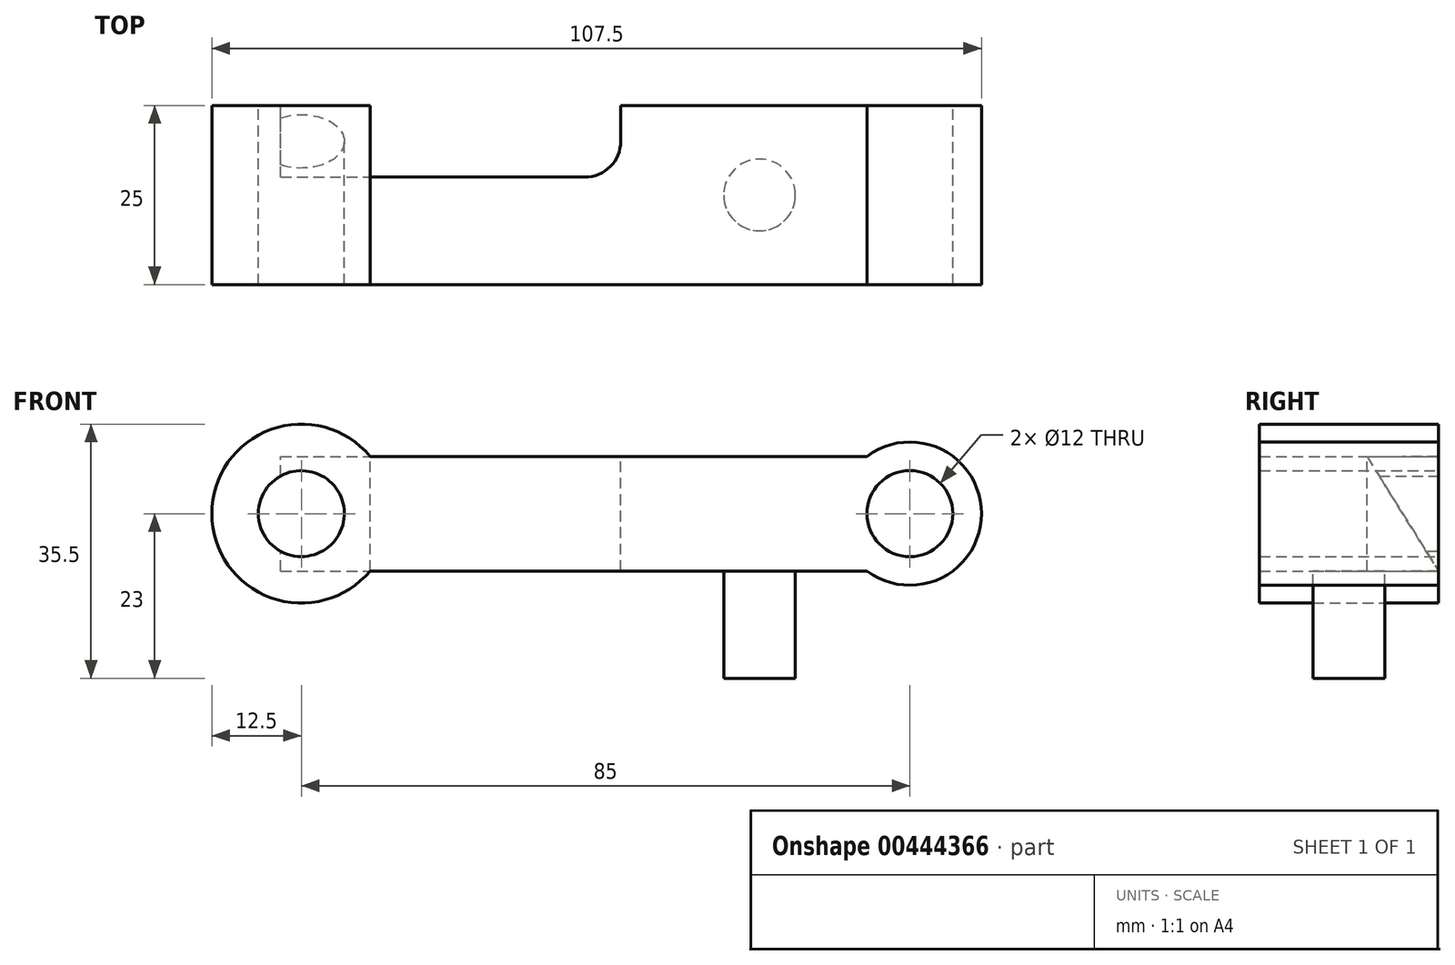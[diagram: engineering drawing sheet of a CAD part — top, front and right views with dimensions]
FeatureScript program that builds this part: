
annotation { "Feature Type Name" : "Feature", "Feature Type Description" : "" }
export const myFeature = defineFeature(function(context is Context, id is Id, definition is map)
    precondition{}
    {
        {
            var Q0;
            Q0=qCreatedBy(makeId("Front.planeOp"),FACE);
            var sketch = newSketch(context, id + "F0", { "sketchPlane" : qUnion([Q0])});
            skCircle(sketch, "E0", {"center": v(0, 0) * mm, "radius": 12.5 * mm});
            skCircle(sketch, "E1", {"center": v(85, 0) * mm, "radius": 10 * mm});
            skLineSegment(sketch, "E2", {"start": v(0, 0) * mm, "end": v(85, 0) * mm, "construction": true});
            skLineSegment(sketch, "E3", {"start": v(9.6, 8) * mm, "end": v(79, 8) * mm});
            skLineSegment(sketch, "E4.MirrorCS", {"start": v(9.6, -8) * mm, "end": v(79, -8) * mm});
            skCircle(sketch, "E5", {"center": v(0, 0) * mm, "radius": 6 * mm});
            skCircle(sketch, "E6", {"center": v(85, 0) * mm, "radius": 6 * mm});
            skSolve(sketch);
        }
        {
            var Q0;
            Q0 = qSketchRegion(id + "F0", true);
            extrude(context, id + "F1", {"entities" : qUnion([Q0]), "depth" : 25 * mm});
        }
        {
            var Q0;
            Q0=makeQuery(id+"F1.opExtrude","SWEPT_FACE",FACE,{"disambiguationData":[OSD([sQuery(id+"F0.wireOp",EDGE,"E3")])]});
            var sketch = newSketch(context, id + "F2", { "sketchPlane" : qUnion([Q0])});
            skLineSegment(sketch, "E7.bottom", {"start": v(9.6, 0) * mm, "end": v(44.6, 0) * mm});
            skLineSegment(sketch, "E7.top", {"start": v(9.6, -10) * mm, "end": v(44.6, -10) * mm});
            skLineSegment(sketch, "E7.left", {"start": v(9.6, 0) * mm, "end": v(9.6, -10) * mm});
            skLineSegment(sketch, "E7.right", {"start": v(44.6, 0) * mm, "end": v(44.6, -10) * mm});
            skSolve(sketch);
        }
        {
            var Q0;
            Q0=makeQuery(id+"F2.imprint","IMPRINT",FACE,{"disambiguationData":[TD([[makeQuery(id+"F2.imprint","IMPRINT",EDGE,{"derivedFrom":sQuery(id+"F2.wireOp",EDGE,"E7.bottom")}),-1.0]])]});
            extrude(context, id + "F3", {"entities" : qUnion([Q0]), "operationType" : NewBodyOperationType.REMOVE, "endBound" : BoundingType.THROUGH_ALL, "oppositeDirection" : true, "depth" : 25 * mm});
        }
        {
            var Q0;
            Q0=makeQuery(id+"F3.boolean.opBoolean","COPY",FACE,{"derivedFrom":makeQuery(id+"F3.opExtrude","SWEPT_FACE",FACE,{"disambiguationData":[OSD([sQuery(id+"F2.wireOp",EDGE,"E7.left")])]})});
            var sketch = newSketch(context, id + "F4", { "sketchPlane" : qUnion([Q0])});
            skLineSegment(sketch, "E8", {"start": v(-10, 8) * mm, "end": v(0, -8) * mm});
            skSolve(sketch);
        }
        {
            var Q0;
            Q0=makeQuery(id+"F4.imprint","IMPRINT",FACE,{"disambiguationData":[TD([[makeQuery(id+"F4.imprint","IMPRINT",EDGE,{"derivedFrom":sQuery(id+"F4.wireOp",EDGE,"E8")}),1.0]])]});
            extrude(context, id + "F5", {"entities" : qUnion([Q0]), "operationType" : NewBodyOperationType.REMOVE, "endBound" : BoundingType.SYMMETRIC, "oppositeDirection" : true, "depth" : 25 * mm});
        }
        {
            var Q0;
            Q0=makeQuery(id+"F3.boolean.opBoolean","COPY",EDGE,{"derivedFrom":makeQuery(id+"F3.opExtrude","SWEPT_EDGE",EDGE,{"disambiguationData":[OSD([sQuery(id+"F2.wireOp",EDGE,"E7.top"),sQuery(id+"F2.wireOp",EDGE,"E7.right")])]})});
            fillet(context, id + "F6", {"entities" : qUnion([Q0]), "radius" : 5 * mm, "tangentPropagation" : true, "allowEdgeOverflow" : false});
        }
        {
            var Q0;
            Q0=makeQuery(id+"F1.opExtrude","SWEPT_FACE",FACE,{"disambiguationData":[OSD([sQuery(id+"F0.wireOp",EDGE,"E4.MirrorCS")])]});
            var sketch = newSketch(context, id + "F7", { "sketchPlane" : qUnion([Q0])});
            skCircle(sketch, "E9", {"center": v(64, 12.5) * mm, "radius": 5 * mm});
            skSolve(sketch);
        }
        {
            var Q0;
            Q0=makeQuery(id+"F7.imprint","IMPRINT",FACE,{"disambiguationData":[TD([[makeQuery(id+"F7.imprint","IMPRINT",EDGE,{"derivedFrom":sQuery(id+"F7.wireOp",EDGE,"E9")}),1.0]])]});
            extrude(context, id + "F8", {"entities" : qUnion([Q0]), "operationType" : NewBodyOperationType.ADD, "depth" : 15 * mm});
        }
    });
